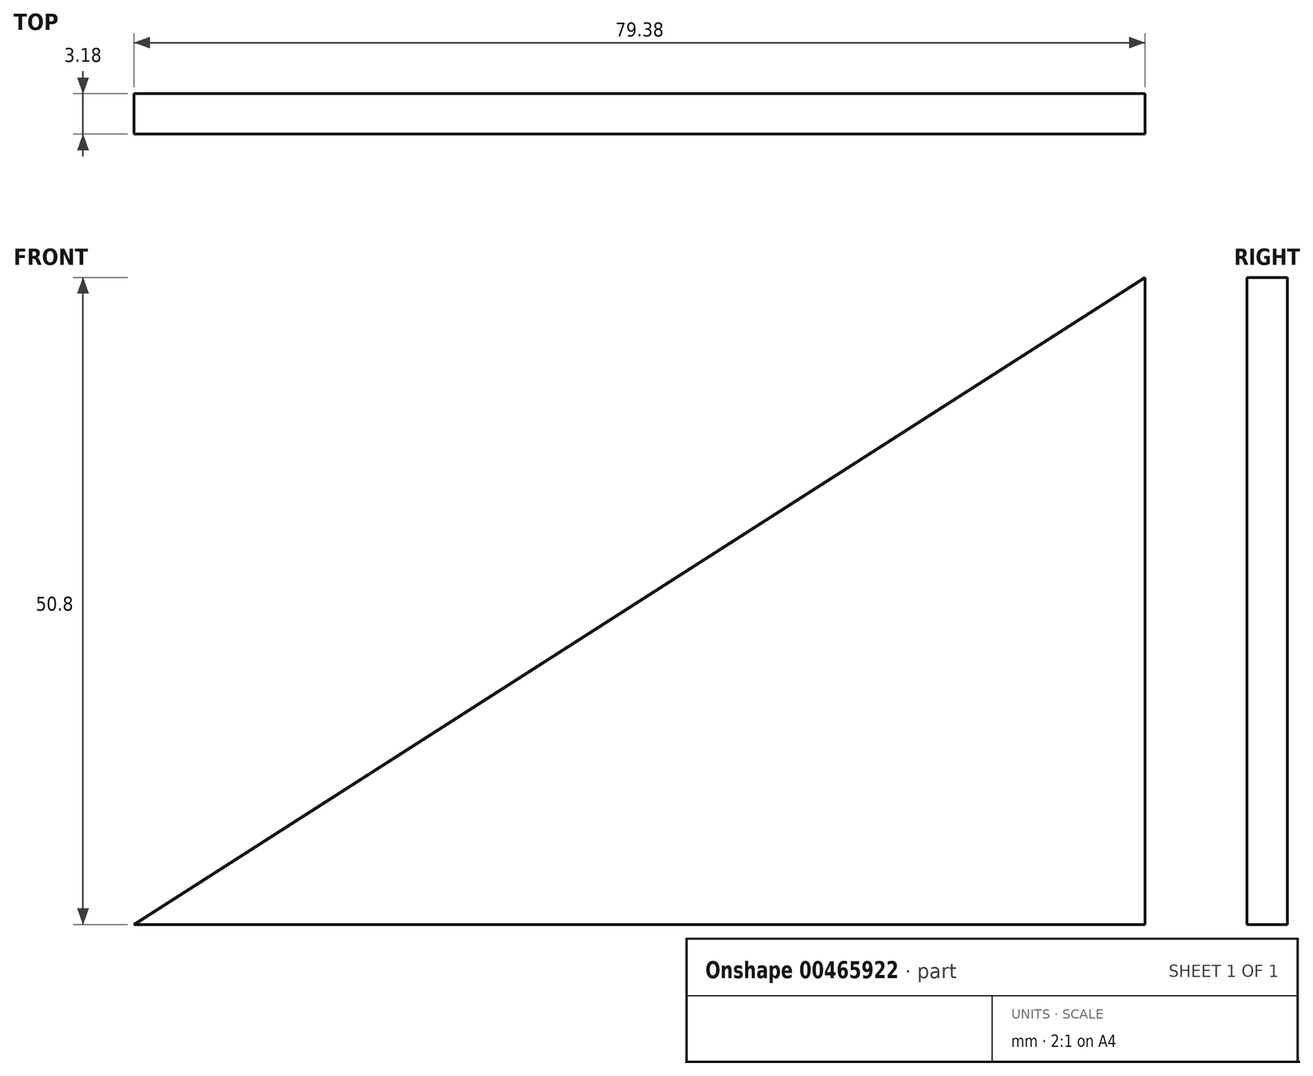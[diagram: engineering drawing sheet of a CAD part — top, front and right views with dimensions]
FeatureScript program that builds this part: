
annotation { "Feature Type Name" : "Feature", "Feature Type Description" : "" }
export const myFeature = defineFeature(function(context is Context, id is Id, definition is map)
    precondition{}
    {
        {
            var Q0;
            Q0=qCreatedBy(makeId("Front.planeOp"),FACE);
            var sketch = newSketch(context, id + "F0", { "sketchPlane" : qUnion([Q0])});
            skLineSegment(sketch, "E0.bottom", {"start": v(-39.69, 25.4) * mm, "end": v(39.69, 25.4) * mm});
            skLineSegment(sketch, "E0.top", {"start": v(-39.69, -25.4) * mm, "end": v(39.69, -25.4) * mm});
            skLineSegment(sketch, "E0.left", {"start": v(-39.69, 25.4) * mm, "end": v(-39.69, -25.4) * mm});
            skLineSegment(sketch, "E0.right", {"start": v(39.69, 25.4) * mm, "end": v(39.69, -25.4) * mm});
            skPoint(sketch, "E0.middle", {"position": v(0, 0) * mm});
            skLineSegment(sketch, "E1", {"start": v(-39.69, -25.4) * mm, "end": v(39.69, 25.4) * mm});
            skSolve(sketch);
        }
        {
            var Q0;
            Q0=makeQuery(id+"F0.imprint","IMPRINT",FACE,{"disambiguationData":[TD([[makeQuery(id+"F0.imprint","IMPRINT",EDGE,{"derivedFrom":sQuery(id+"F0.wireOp",EDGE,"E0.top")}),1.0]])]});
            extrude(context, id + "F1", {"entities" : qUnion([Q0]), "endBound" : BoundingType.SYMMETRIC, "depth" : 3.17 * mm});
        }
    });
